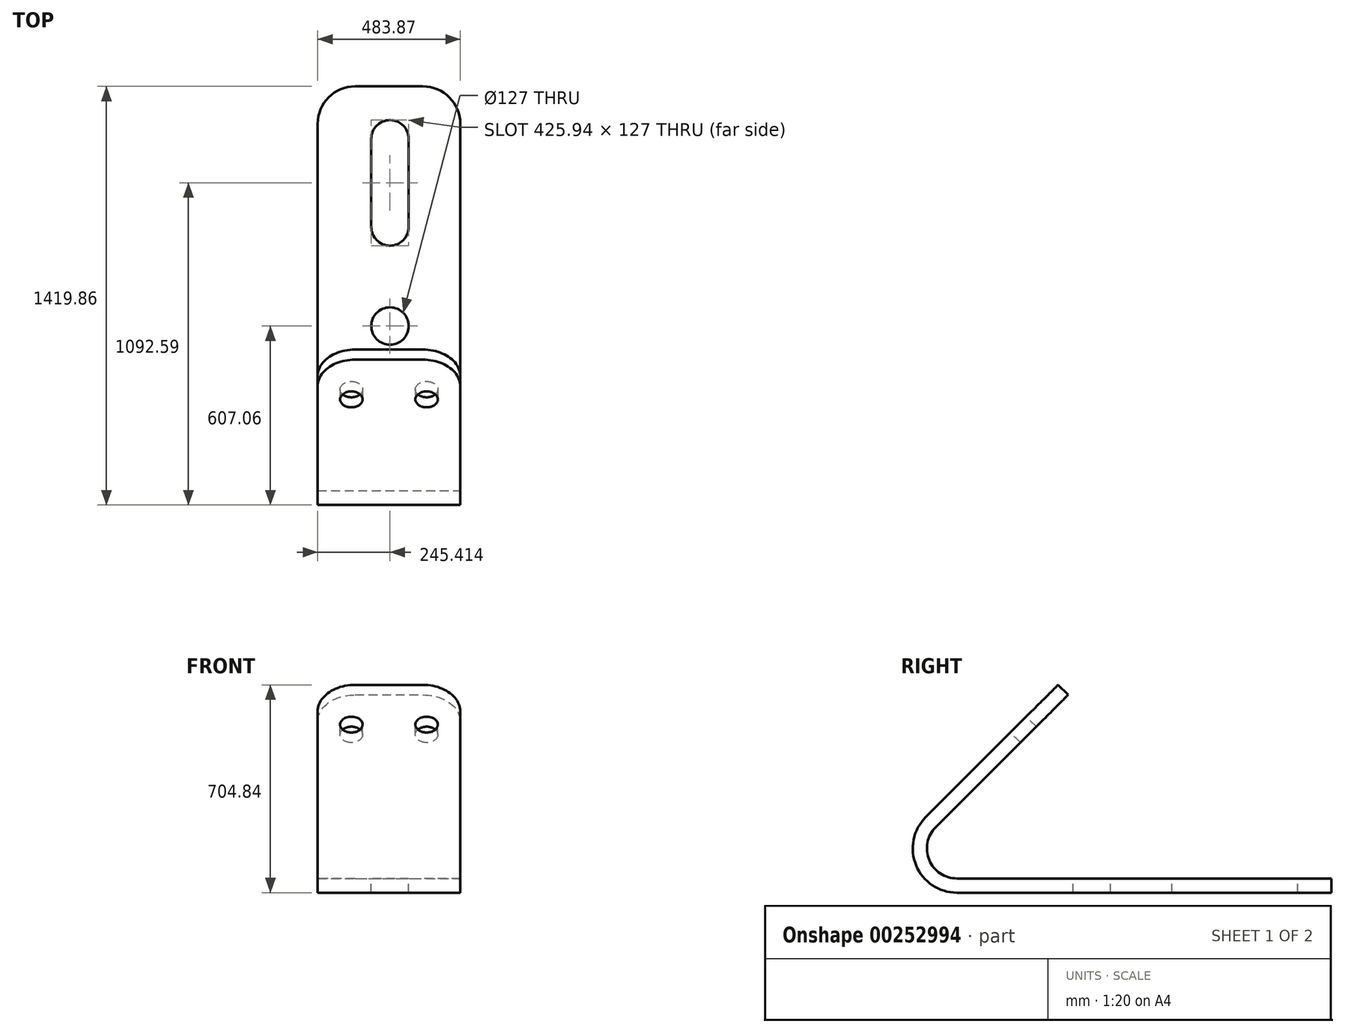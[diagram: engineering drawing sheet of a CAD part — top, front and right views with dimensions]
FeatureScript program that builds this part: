
annotation { "Feature Type Name" : "Feature", "Feature Type Description" : "" }
export const myFeature = defineFeature(function(context is Context, id is Id, definition is map)
    precondition{}
    {
        {
            var Q0;
            Q0=qCreatedBy(makeId("Right.planeOp"),FACE);
            var sketch = newSketch(context, id + "F0", { "sketchPlane" : qUnion([Q0])});
            skLineSegment(sketch, "E0", {"start": v(-635, 0) * mm, "end": v(635, 0) * mm});
            skLineSegment(sketch, "E1", {"start": v(-706.84, 173.44) * mm, "end": v(-257.83, 622.45) * mm});
            skArc(sketch, "E2", {"start": v(-706.84, 173.44) * mm, "mid": v(-728.87, 62.72) * mm, "end": v(-635, 0) * mm});
            skLineSegment(sketch, "E3.0", {"start": v(-635, -48.26) * mm, "end": v(635, -48.26) * mm});
            skArc(sketch, "E3.1", {"start": v(-740.97, 207.57) * mm, "mid": v(-773.45, 44.25) * mm, "end": v(-635, -48.26) * mm});
            skLineSegment(sketch, "E3.2", {"start": v(-740.97, 207.57) * mm, "end": v(-291.95, 656.58) * mm});
            skLineSegment(sketch, "E4", {"start": v(635, 0) * mm, "end": v(635, -48.26) * mm});
            skLineSegment(sketch, "E5", {"start": v(-291.95, 656.58) * mm, "end": v(-257.83, 622.45) * mm});
            skSolve(sketch);
        }
        {
            var Q0;
            Q0=qSketchRegion(id+"F0",true);
            extrude(context, id + "F1", {"entities" : qUnion([Q0]), "oppositeDirection" : true, "depth" : 483.87 * mm});
        }
        {
            var Q0;
            Q0=makeQuery(id+"F1.opExtrude","SWEPT_FACE",FACE,{"disambiguationData":[OSD([sQuery(id+"F0.wireOp",EDGE,"E0")])]});
            var sketch = newSketch(context, id + "F2", { "sketchPlane" : qUnion([Q0])});
            skCircle(sketch, "E6", {"center": v(-238.46, -177.8) * mm, "radius": 63.5 * mm});
            skLineSegment(sketch, "E7", {"start": v(-238.46, -177.8) * mm, "end": v(-238.46, 457.2) * mm, "construction": true});
            skArc(sketch, "E8", {"start": v(-174.96, 457.2) * mm, "mid": v(-238.46, 520.7) * mm, "end": v(-301.96, 457.2) * mm});
            skArc(sketch, "E9", {"start": v(-301.96, 158.26) * mm, "mid": v(-238.46, 94.76) * mm, "end": v(-174.96, 158.26) * mm});
            skLineSegment(sketch, "E10", {"start": v(-301.96, 158.26) * mm, "end": v(-301.96, 457.2) * mm});
            skLineSegment(sketch, "E11", {"start": v(-174.96, 158.26) * mm, "end": v(-174.96, 457.2) * mm});
            skPoint(sketch, "E12.end.orphan", {"position": v(-238.46, 520.7) * mm});
            skSolve(sketch);
        }
        {
            var Q0;
            Q0=qSketchRegion(id+"F2",true);
            extrude(context, id + "F3", {"entities" : qUnion([Q0]), "operationType" : NewBodyOperationType.REMOVE, "endBound" : BoundingType.THROUGH_ALL, "oppositeDirection" : true, "depth" : 25.4 * mm});
        }
        {
            var Q0;
            Q0=makeQuery(id+"F1.opExtrude","SWEPT_FACE",FACE,{"disambiguationData":[OSD([sQuery(id+"F0.wireOp",EDGE,"E3.2")])]});
            var sketch = newSketch(context, id + "F4", { "sketchPlane" : qUnion([Q0])});
            skCircle(sketch, "E13", {"center": v(-369.57, 67.33) * mm, "radius": 38.1 * mm});
            skCircle(sketch, "E14", {"center": v(-114.3, 67.33) * mm, "radius": 38.1 * mm});
            skSolve(sketch);
        }
        {
            var Q0;
            Q0=qSketchRegion(id+"F4",true);
            var Q1;
            Q1=makeQuery(id+"F1.opExtrude","SWEPT_FACE",FACE,{"disambiguationData":[OSD([sQuery(id+"F0.wireOp",EDGE,"E1")])]});
            extrude(context, id + "F5", {"entities" : qUnion([Q0]), "operationType" : NewBodyOperationType.REMOVE, "endBound" : BoundingType.UP_TO_SURFACE, "oppositeDirection" : true, "endBoundEntityFace" : qUnion([Q1]), "depth" : 76.2 * mm});
        }
        {
            var Q0;
            Q0=makeQuery(id+"F1.opExtrude","SWEPT_FACE",FACE,{"disambiguationData":[OSD([sQuery(id+"F0.wireOp",EDGE,"E0")])]});
            var sketch = newSketch(context, id + "F6", { "sketchPlane" : qUnion([Q0])});
            skLineSegment(sketch, "E15.0", {"start": v(0, -635) * mm, "end": v(0, 508) * mm});
            skLineSegment(sketch, "E16.0", {"start": v(-356.87, 635) * mm, "end": v(-127, 635) * mm});
            skLineSegment(sketch, "E17.0", {"start": v(-483.87, -635) * mm, "end": v(-483.87, 508) * mm});
            skPoint(sketch, "E18.visualSharp", {"position": v(0, 635) * mm});
            skArc(sketch, "E18.filletArc", {"start": v(0, 508) * mm, "mid": v(-37.2, 597.8) * mm, "end": v(-127, 635) * mm});
            skPoint(sketch, "E19.visualSharp", {"position": v(-483.87, 635) * mm});
            skArc(sketch, "E19.filletArc", {"start": v(-356.87, 635) * mm, "mid": v(-446.67, 597.8) * mm, "end": v(-483.87, 508) * mm});
            skSolve(sketch);
        }
        {
            var Q0;
            {var subQ0=sQuery(id+"F6.wireOp",EDGE,"E18.filletArc");Q0=makeQuery(id+"F6.imprint","IMPRINT",FACE,{"disambiguationData":[TD([[makeQuery(id+"F6.imprint","IMPRINT",EDGE,{"derivedFrom":subQ0}),-1.0]])]});}
            var Q1;
            {var subQ0=sQuery(id+"F6.wireOp",EDGE,"E19.filletArc");Q1=makeQuery(id+"F6.imprint","IMPRINT",FACE,{"disambiguationData":[TD([[makeQuery(id+"F6.imprint","IMPRINT",EDGE,{"derivedFrom":subQ0}),-1.0]])]});}
            extrude(context, id + "F7", {"entities" : qUnion([Q0, Q1]), "operationType" : NewBodyOperationType.REMOVE, "endBound" : BoundingType.THROUGH_ALL, "oppositeDirection" : true, "depth" : 25.4 * mm});
        }
        {
            var Q0;
            Q0=makeQuery(id+"F1.opExtrude","SWEPT_FACE",FACE,{"disambiguationData":[OSD([sQuery(id+"F0.wireOp",EDGE,"E3.2")])]});
            var sketch = newSketch(context, id + "F8", { "sketchPlane" : qUnion([Q0])});
            skLineSegment(sketch, "E20.0", {"start": v(-356.87, 257.83) * mm, "end": v(-127, 257.83) * mm});
            skLineSegment(sketch, "E21.0", {"start": v(-483.87, -377.17) * mm, "end": v(-483.87, 130.83) * mm});
            skLineSegment(sketch, "E22.0", {"start": v(0, -377.17) * mm, "end": v(0, 130.83) * mm});
            skPoint(sketch, "E23.visualSharp", {"position": v(-483.87, 257.83) * mm});
            skArc(sketch, "E23.filletArc", {"start": v(-356.87, 257.83) * mm, "mid": v(-446.67, 220.63) * mm, "end": v(-483.87, 130.83) * mm});
            skPoint(sketch, "E24.visualSharp", {"position": v(0, 257.83) * mm});
            skArc(sketch, "E24.filletArc", {"start": v(0, 130.83) * mm, "mid": v(-37.2, 220.63) * mm, "end": v(-127, 257.83) * mm});
            skSolve(sketch);
        }
        {
            var Q0;
            {var subQ0=sQuery(id+"F8.wireOp",EDGE,"E23.filletArc");Q0=makeQuery(id+"F8.imprint","IMPRINT",FACE,{"disambiguationData":[TD([[makeQuery(id+"F8.imprint","IMPRINT",EDGE,{"derivedFrom":subQ0}),-1.0]])]});}
            var Q1;
            {var subQ0=sQuery(id+"F8.wireOp",EDGE,"E24.filletArc");Q1=makeQuery(id+"F8.imprint","IMPRINT",FACE,{"disambiguationData":[TD([[makeQuery(id+"F8.imprint","IMPRINT",EDGE,{"derivedFrom":subQ0}),-1.0]])]});}
            extrude(context, id + "F9", {"entities" : qUnion([Q0, Q1]), "operationType" : NewBodyOperationType.REMOVE, "endBound" : BoundingType.UP_TO_NEXT, "oppositeDirection" : true, "depth" : 25.4 * mm});
        }
    });
